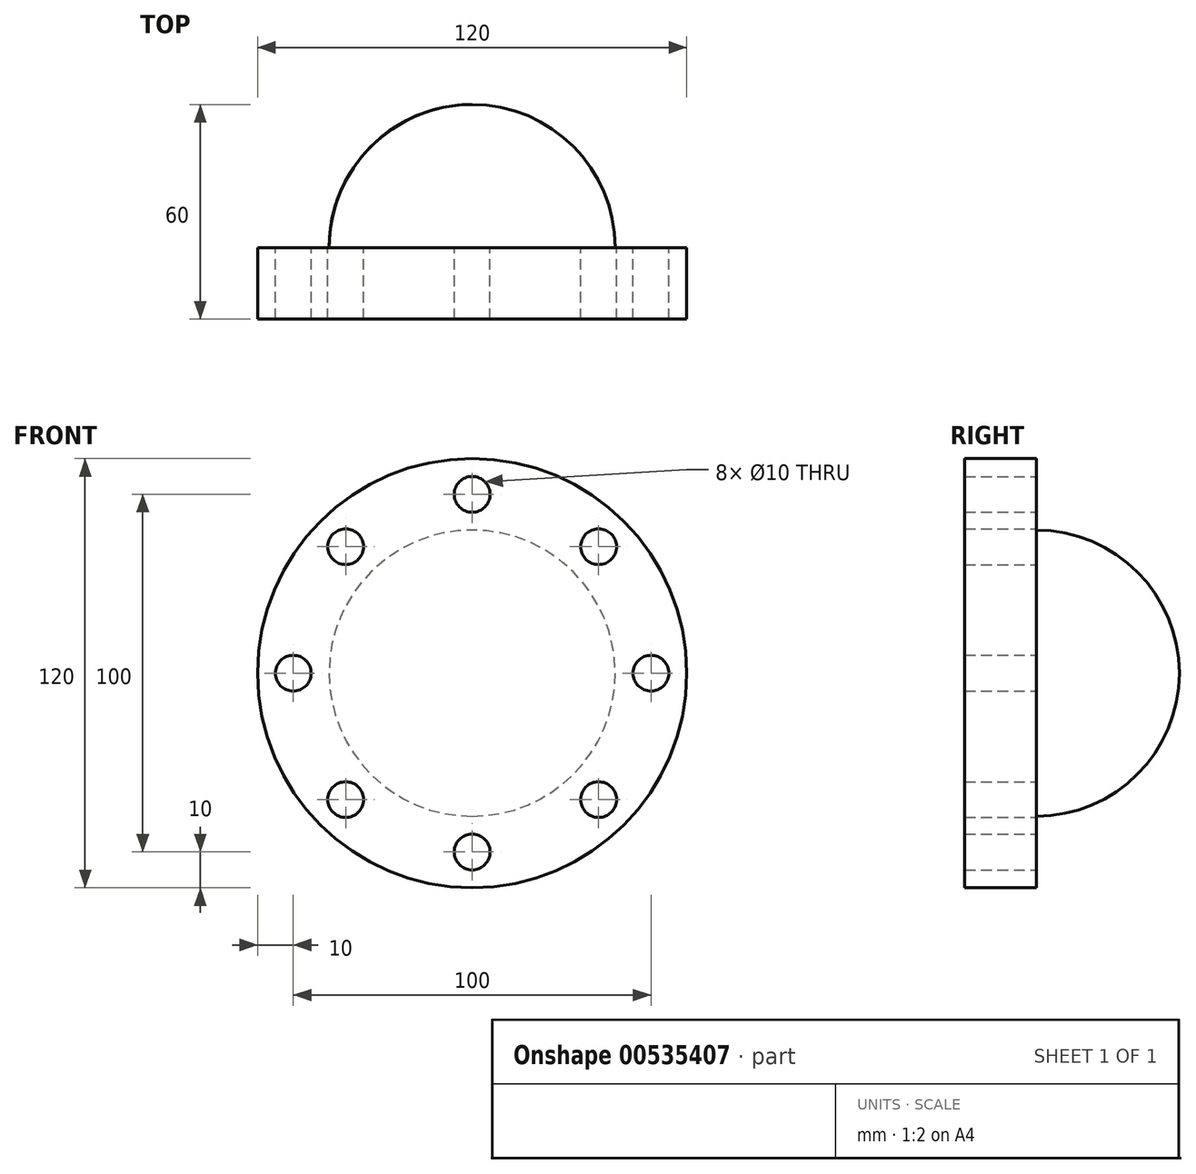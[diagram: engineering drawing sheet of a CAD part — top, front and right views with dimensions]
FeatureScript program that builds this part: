
annotation { "Feature Type Name" : "Feature", "Feature Type Description" : "" }
export const myFeature = defineFeature(function(context is Context, id is Id, definition is map)
    precondition{}
    {
        {
            var Q0;
            Q0=qCreatedBy(makeId("Front.planeOp"),FACE);
            var sketch = newSketch(context, id + "F0", { "sketchPlane" : qUnion([Q0])});
            skCircle(sketch, "E0", {"center": v(0, 0) * mm, "radius": 60 * mm});
            skCircle(sketch, "E1", {"center": v(0, 50) * mm, "radius": 5 * mm});
            skCircle(sketch, "E2.1.0", {"center": v(-35.36, 35.36) * mm, "radius": 5 * mm});
            skCircle(sketch, "E2.2.0", {"center": v(-50, 0) * mm, "radius": 5 * mm});
            skCircle(sketch, "E3.1.3.0", {"center": v(-35.36, -35.36) * mm, "radius": 5 * mm});
            skCircle(sketch, "E3.1.4.0", {"center": v(0, -50) * mm, "radius": 5 * mm});
            skCircle(sketch, "E3.1.5.0", {"center": v(35.36, -35.36) * mm, "radius": 5 * mm});
            skCircle(sketch, "E3.1.6.0", {"center": v(50, 0) * mm, "radius": 5 * mm});
            skCircle(sketch, "E3.1.7.0", {"center": v(35.36, 35.36) * mm, "radius": 5 * mm});
            skSolve(sketch);
        }
        {
            var Q0;
            Q0 = qSketchRegion(id + "F0", true);
            extrude(context, id + "F1", {"entities" : qUnion([Q0]), "depth" : 20 * mm, "offsetDistance" : 25 * mm});
        }
        {
            var Q0;
            Q0=qCreatedBy(makeId("Top.planeOp"),FACE);
            var sketch = newSketch(context, id + "F2", { "sketchPlane" : qUnion([Q0])});
            skLineSegment(sketch, "E4.0", {"start": v(0, 0) * mm, "end": v(-60, 0) * mm});
            skLineSegment(sketch, "E5", {"start": v(60, 0) * mm, "end": v(60, -20) * mm});
            skLineSegment(sketch, "E6", {"start": v(-60, -20) * mm, "end": v(-60, 0) * mm});
            skArc(sketch, "E7", {"start": v(0, 40) * mm, "mid": v(-28.28, 28.28) * mm, "end": v(-40, 0) * mm});
            skLineSegment(sketch, "E8", {"start": v(0, 0) * mm, "end": v(0, 40) * mm});
            skPoint(sketch, "E9.orphan", {"position": v(60, 0) * mm});
            skSolve(sketch);
        }
        {
            var Q0;
            {var subQ2=sQuery(id+"F2.wireOp",EDGE,"E7");Q0=makeQuery(id+"F2.imprint","IMPRINT",FACE,{"disambiguationData":[TD([[makeQuery(id+"F2.imprint","IMPRINT",EDGE,{"derivedFrom":subQ2}),1.0]])]});}
            var Q1;
            Q1=sQuery(id+"F2.wireOp",EDGE,"E8");
            revolve(context, id + "F3", {"operationType" : NewBodyOperationType.ADD, "entities" : qUnion([Q0]), "axis" : qUnion([Q1]), "revolveType" : RevolveType.FULL});
        }
    });
